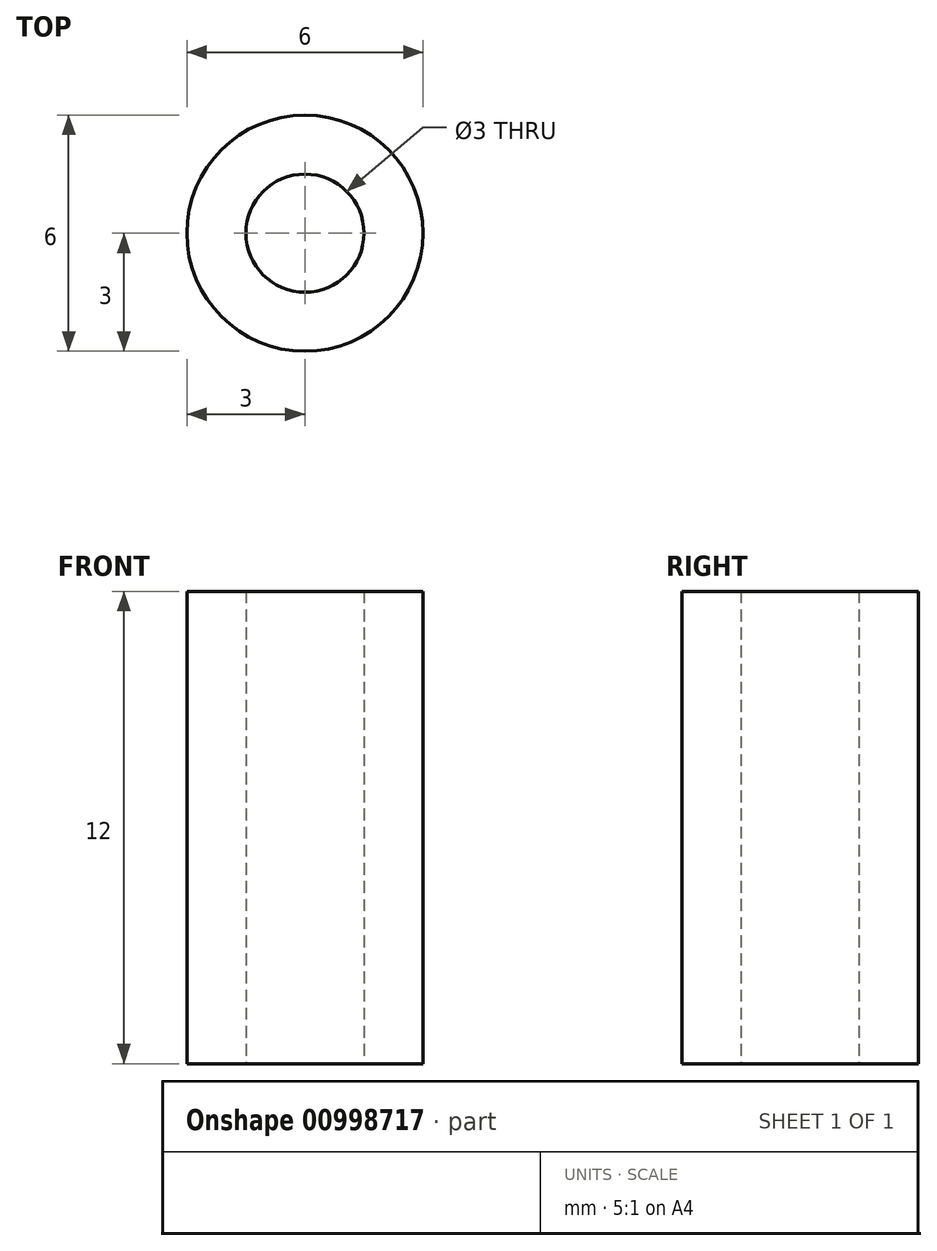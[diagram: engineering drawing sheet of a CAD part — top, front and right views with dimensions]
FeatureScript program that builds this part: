
annotation { "Feature Type Name" : "Feature", "Feature Type Description" : "" }
export const myFeature = defineFeature(function(context is Context, id is Id, definition is map)
    precondition{}
    {
        {
            var Q0;
            Q0=qCreatedBy(makeId("Top.planeOp"),FACE);
            var sketch = newSketch(context, id + "F0", { "sketchPlane" : qUnion([Q0])});
            skCircle(sketch, "E0", {"center": v(0, 0) * mm, "radius": 1.5 * mm});
            skCircle(sketch, "E1", {"center": v(0, 0) * mm, "radius": 3 * mm});
            skSolve(sketch);
        }
        {
            var Q0;
            Q0 = qSketchRegion(id + "F0", true);
            extrude(context, id + "F1", {"entities" : qUnion([Q0]), "endBound" : BoundingType.SYMMETRIC, "depth" : 12 * mm, "offsetDistance" : 25 * mm});
        }
    });
